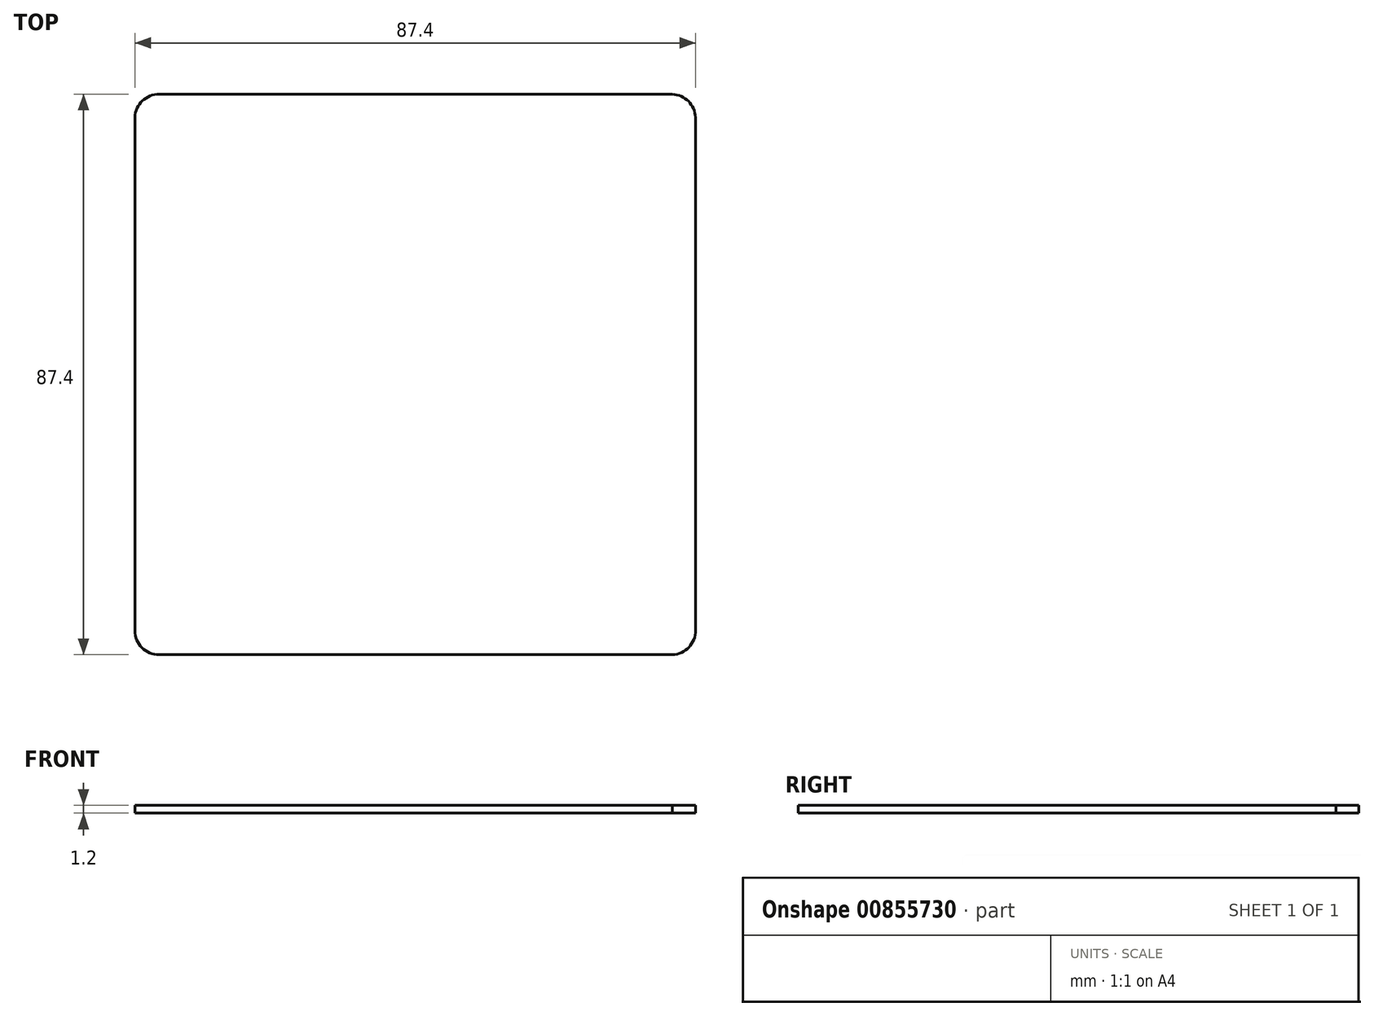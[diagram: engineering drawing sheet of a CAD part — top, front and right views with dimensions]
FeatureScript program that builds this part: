
annotation { "Feature Type Name" : "Feature", "Feature Type Description" : "" }
export const myFeature = defineFeature(function(context is Context, id is Id, definition is map)
    precondition{}
    {
        {
            var Q0;
            Q0=qCreatedBy(makeId("Top.planeOp"),FACE);
            var sketch = newSketch(context, id + "F0", { "sketchPlane" : qUnion([Q0])});
            skLineSegment(sketch, "E0.0", {"start": v(80, 83.6) * mm, "end": v(0, 83.6) * mm});
            skArc(sketch, "E1.0", {"start": v(80, 83.6) * mm, "mid": v(82.5, 82.5) * mm, "end": v(83.6, 80) * mm});
            skLineSegment(sketch, "E2.0", {"start": v(83.6, 80) * mm, "end": v(83.6, 0) * mm});
            skArc(sketch, "E3.0", {"start": v(83.6, 0) * mm, "mid": v(82.56, -2.62) * mm, "end": v(80, -3.8) * mm});
            skLineSegment(sketch, "E4.0", {"start": v(80, -3.8) * mm, "end": v(0, -3.8) * mm});
            skArc(sketch, "E5.0", {"start": v(0, -3.8) * mm, "mid": v(-2.69, -2.69) * mm, "end": v(-3.8, 0) * mm});
            skLineSegment(sketch, "E6.0", {"start": v(-3.8, 80) * mm, "end": v(-3.8, 0) * mm});
            skArc(sketch, "E7.0", {"start": v(-3.8, 80) * mm, "mid": v(-2.62, 82.56) * mm, "end": v(0, 83.6) * mm});
            skSolve(sketch);
        }
        {
            var Q0;
            Q0 = qSketchRegion(id + "F0", true);
            extrude(context, id + "F1", {"entities" : qUnion([Q0]), "depth" : 1.2 * mm, "offsetDistance" : 25 * mm});
        }
    });
